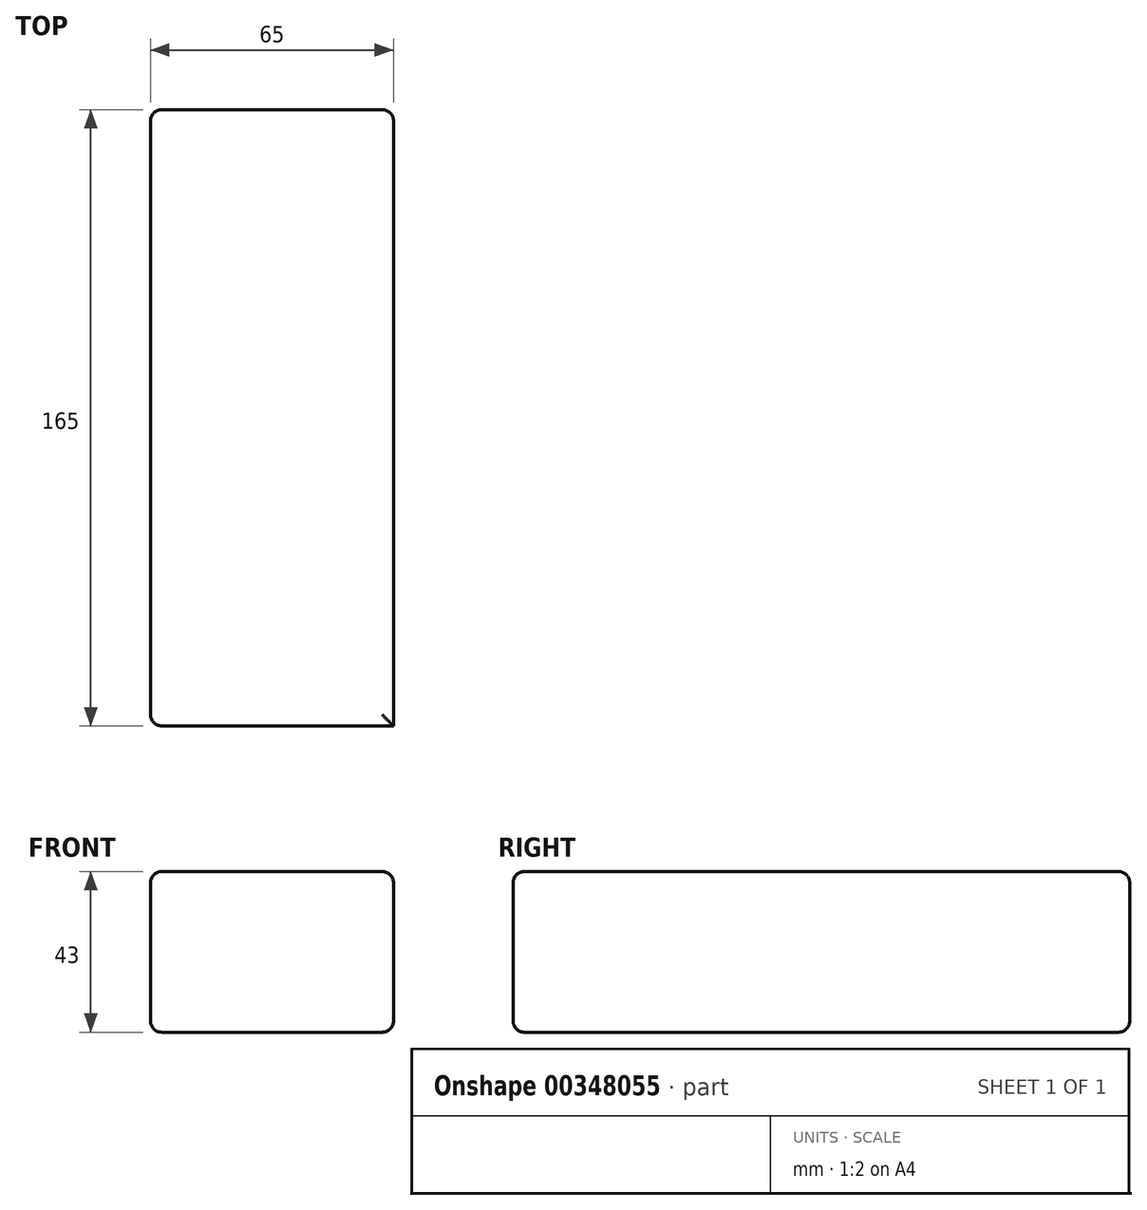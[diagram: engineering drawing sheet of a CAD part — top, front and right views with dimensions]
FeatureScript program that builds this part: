
annotation { "Feature Type Name" : "Feature", "Feature Type Description" : "" }
export const myFeature = defineFeature(function(context is Context, id is Id, definition is map)
    precondition{}
    {
        {
            var Q0;
            Q0=qCreatedBy(makeId("Top.planeOp"),FACE);
            var sketch = newSketch(context, id + "F0", { "sketchPlane" : qUnion([Q0])});
            skLineSegment(sketch, "E0.bottom", {"start": v(-32.5, 82.5) * mm, "end": v(32.5, 82.5) * mm});
            skLineSegment(sketch, "E0.top", {"start": v(-32.5, -82.5) * mm, "end": v(32.5, -82.5) * mm});
            skLineSegment(sketch, "E0.left", {"start": v(-32.5, 82.5) * mm, "end": v(-32.5, -82.5) * mm});
            skLineSegment(sketch, "E0.right", {"start": v(32.5, 82.5) * mm, "end": v(32.5, -82.5) * mm});
            skPoint(sketch, "E0.middle", {"position": v(0, 0) * mm});
            skSolve(sketch);
        }
        {
            var Q0;
            Q0=makeQuery(id+"F0.imprint","IMPRINT",FACE,{"disambiguationData":[TD([[makeQuery(id+"F0.imprint","IMPRINT",EDGE,{"derivedFrom":sQuery(id+"F0.wireOp",EDGE,"E0.bottom")}),-1.0]])]});
            extrude(context, id + "F1", {"entities" : qUnion([Q0]), "depth" : 43 * mm, "offsetDistance" : 25 * mm});
        }
        {
            var Q0;
            Q0=makeQuery(id+"F1.opExtrude","SWEPT_FACE",FACE,{"disambiguationData":[OSD([sQuery(id+"F0.wireOp",EDGE,"E0.left")])]});
            var Q1;
            Q1=makeQuery(id+"F1.opExtrude","CAP_FACE",FACE,{"disambiguationData":[OSD([sQuery(id+"F0.wireOp",EDGE,"E0.bottom"),sQuery(id+"F0.wireOp",EDGE,"E0.top"),sQuery(id+"F0.wireOp",EDGE,"E0.left"),sQuery(id+"F0.wireOp",EDGE,"E0.right")])],"isStart":false});
            var Q2;
            Q2=makeQuery(id+"F1.opExtrude","SWEPT_FACE",FACE,{"disambiguationData":[OSD([sQuery(id+"F0.wireOp",EDGE,"E0.bottom")])]});
            var Q3;
            Q3=makeQuery(id+"F1.opExtrude","CAP_FACE",FACE,{"disambiguationData":[OSD([sQuery(id+"F0.wireOp",EDGE,"E0.bottom"),sQuery(id+"F0.wireOp",EDGE,"E0.top"),sQuery(id+"F0.wireOp",EDGE,"E0.left"),sQuery(id+"F0.wireOp",EDGE,"E0.right")])],"isStart":true});
            fillet(context, id + "F2", {"entities" : qUnion([Q0, Q1, Q2, Q3]), "radius" : 3 * mm, "tangentPropagation" : true, "allowEdgeOverflow" : false});
        }
    });
